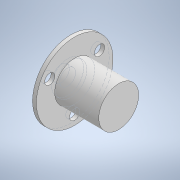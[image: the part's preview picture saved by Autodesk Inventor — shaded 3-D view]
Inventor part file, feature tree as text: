
AUTODESK INVENTOR PART (.ipt)
format: ipt  version: 2022 (Build 260153070, 153G)  size: 143,872 bytes
history: native  units: mm
features: sketch x4, extrude x3, revolve x1
ambient origin geometry x8: Origin, YZ Plane, XZ Plane, XY Plane, X Axis, Y Axis, Z Axis, Center Point
bodies: Solid1 (feature_tree)
feature tree (8):
  revolve  "Revolution1"  [1 undecoded]
  extrude  "Extrusion1"  Depth=12.0mm
  extrude  "Extrusion2"  Depth=1.5mm
  extrude  "Extrusion3"  Depth=18.0mm
  sketch  "Sketch1"  dims[d0=6.25mm d1=15.0mm]
  sketch  "Sketch2"  dims[d2=1.2mm d3=12.0mm]
  sketch  "Sketch3"  dims[d4=2.5mm d5=1.5mm]
  sketch  "Sketch4"  dims[d6=90.0deg d7=18.0mm d8=3.2mm d9=30.0mm d11=360.0deg d13=1.2mm d14=0.0mm d15=1.5mm d16=0.0mm d17=10.0mm d18=1.0mm d19=0.0mm]
note: 1 required parameter value undecoded (feature->parameter linkage not recoverable at this tier; creation-order binding heuristic only, values carry confidence <= 0.55)
